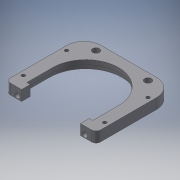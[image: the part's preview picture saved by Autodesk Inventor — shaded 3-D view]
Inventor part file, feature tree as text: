
AUTODESK INVENTOR PART (.ipt)
format: ipt  version: 2017 (Build 210142000, 142)  size: 204,288 bytes
history: native  units: mm
features: extrude x5, sketch x5, fillet x2, projected_geometry x2, reference x2, other x2, mirror x1
ambient origin geometry x8: Origin, YZ Plane, XZ Plane, XY Plane, X Axis, Y Axis, Z Axis, Center Point
bodies: Solid1 (feature_tree)
feature tree (19):
  extrude  "Extrusion1"  Depth=80.0mm
  extrude  "Extrusion2"  Depth=2.0mm
  extrude  "Extrusion3"  Depth=10.0mm
  extrude  "Extrusion4"  Depth=5.0mm TaperAngle=0.0deg
  extrude  "Extrusion5"  Depth=4.0mm
  mirror  "Mirror1"
  fillet  "Fillet1"  Radius=5.0mm
  fillet  "Fillet2"  Radius=50.0mm
  sketch  "Sketch1"  dims[d0=8.0mm d1=80.0mm]
  sketch  "Sketch2"  dims[d2=2.0mm d3=50.0mm]
  projected_geometry  "Projected Loop1"
  sketch  "Sketch3"  dims[d4=10.0mm d5=40.0mm]
  sketch  "Sketch4"  dims[d6=7.0mm d7=0.0mm d9=5.0mm d10=0.0mm]
  reference  "Reference1"
  reference  "Reference2"
  sketch  "Sketch5"  dims[d11=76.0mm d12=4.0mm d13=5.0mm d14=50.0mm d15=4.0mm d16=0.0mm d17=10.0mm d18=0.0mm d19=6.0mm d20=4.0mm d21=10.0mm d22=0.0mm d23=20.0mm d24=5.0mm]
  projected_geometry  "Projected Loop2"
  other  "peristaltic pump.iam"
  other  "frame bottom:1"
